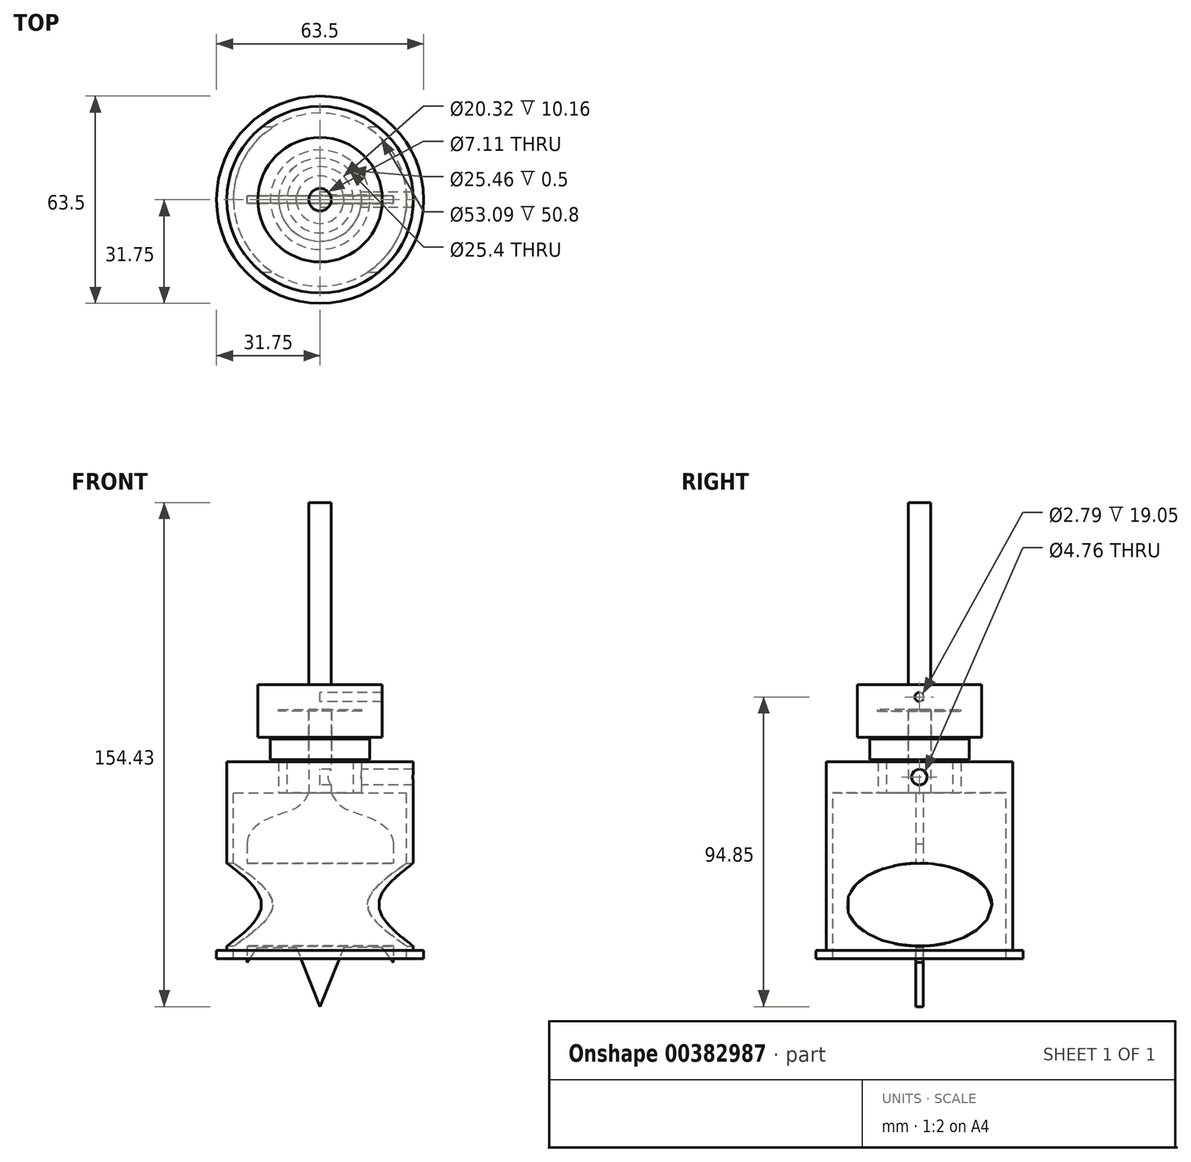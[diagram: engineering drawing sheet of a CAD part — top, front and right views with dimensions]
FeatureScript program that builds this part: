
annotation { "Feature Type Name" : "Feature", "Feature Type Description" : "" }
export const myFeature = defineFeature(function(context is Context, id is Id, definition is map)
    precondition{}
    {
        {
            var Q0;
            Q0=qCreatedBy(makeId("Top.planeOp"),FACE);
            var sketch = newSketch(context, id + "F0", { "sketchPlane" : qUnion([Q0])});
            skCircle(sketch, "E0", {"center": v(0, 0) * mm, "radius": 3.43 * mm});
            skSolve(sketch);
        }
        {
            var Q0;
            Q0 = qSketchRegion(id + "F0", true);
            extrude(context, id + "F1", {"entities" : qUnion([Q0]), "depth" : 50.8 * mm, "hasSecondDirection" : true, "secondDirectionOppositeDirection" : true, "secondDirectionDepth" : 38.1 * mm});
        }
        {
            var Q0;
            Q0=qCreatedBy(makeId("Front.planeOp"),FACE);
            var sketch = newSketch(context, id + "F2", { "sketchPlane" : qUnion([Q0])});
            skLineSegment(sketch, "E1", {"start": v(0, -33.13) * mm, "end": v(0, -75.47) * mm, "construction": true});
            skLineSegment(sketch, "E2.0", {"start": v(-3.43, -38.1) * mm, "end": v(3.43, -38.1) * mm});
            skFitSpline(sketch, "E3", {"points": [v(-3.43, -38.1) * mm, v(-12.95, -44.92) * mm, v(-22.43, -53.7) * mm], "startDerivative": vector(-13.87, -31.28) * mm, "endDerivative": vector(-0.61, -28) * mm});
            skLineSegment(sketch, "E4", {"start": v(-22.43, -53.7) * mm, "end": v(-22.43, -90.1) * mm});
            skLineSegment(sketch, "E5", {"start": v(-22.43, -90.1) * mm, "end": v(-19.06, -85.46) * mm});
            skLineSegment(sketch, "E6", {"start": v(-19.06, -85.46) * mm, "end": v(-7.28, -85.46) * mm});
            skLineSegment(sketch, "E7", {"start": v(-7.28, -85.46) * mm, "end": v(0, -103.63) * mm});
            skLineSegment(sketch, "E8.MirrorCS", {"start": v(7.28, -85.46) * mm, "end": v(0, -103.63) * mm});
            skLineSegment(sketch, "E9.MirrorCS", {"start": v(19.06, -85.46) * mm, "end": v(7.28, -85.46) * mm});
            skFitSpline(sketch, "E10.MirrorCS", {"points": [v(3.43, -38.1) * mm, v(12.95, -44.92) * mm, v(22.43, -53.7) * mm], "startDerivative": vector(13.87, -31.28) * mm, "endDerivative": vector(0.61, -28) * mm});
            skLineSegment(sketch, "E11.MirrorCS", {"start": v(22.43, -53.7) * mm, "end": v(22.43, -90.1) * mm});
            skLineSegment(sketch, "E12.MirrorCS", {"start": v(22.43, -90.1) * mm, "end": v(19.06, -85.46) * mm});
            skSolve(sketch);
        }
        {
            var Q0;
            Q0=makeQuery(id+"F2.imprint","IMPRINT",FACE,{"disambiguationData":[TD([[makeQuery(id+"F2.imprint","IMPRINT",EDGE,{"derivedFrom":sQuery(id+"F2.wireOp",EDGE,"E2.0")}),-1.0]])]});
            extrude(context, id + "F3", {"entities" : qUnion([Q0]), "operationType" : NewBodyOperationType.ADD, "depth" : 1.14 * mm, "hasSecondDirection" : true, "secondDirectionOppositeDirection" : true, "secondDirectionDepth" : 1.14 * mm});
        }
        {
            var Q0;
            Q0=qCreatedBy(makeId("Top.planeOp"),FACE);
            cPlane(context, id + "F4", {"entities" : qUnion([Q0]), "cplaneType" : CPlaneType.OFFSET, "offset" : 38.1 * mm, "oppositeDirection" : true, "width" : 152.4 * mm, "height" : 152.4 * mm});
        }
        {
            var Q0;
            Q0=qCreatedBy(id+"F4.planeOp",FACE);
            var sketch = newSketch(context, id + "F5", { "sketchPlane" : qUnion([Q0])});
            skCircle(sketch, "E13", {"center": v(0, 0) * mm, "radius": 28.58 * mm});
            skCircle(sketch, "E14", {"center": v(0, 0) * mm, "radius": 12.7 * mm});
            skSolve(sketch);
        }
        {
            var Q0;
            Q0=makeQuery(id+"F5.imprint","IMPRINT",FACE,{"disambiguationData":[TD([[makeQuery(id+"F5.imprint","IMPRINT",EDGE,{"derivedFrom":sQuery(id+"F5.wireOp",EDGE,"E13")}),1.0]])]});
            extrude(context, id + "F6", {"entities" : qUnion([Q0]), "depth" : 9.52 * mm});
        }
        {
            var Q0;
            Q0=makeQuery(id+"F6.opExtrude","CAP_FACE",FACE,{"disambiguationData":[OSD([sQuery(id+"F5.wireOp",EDGE,"E13"),sQuery(id+"F5.wireOp",EDGE,"E14")])],"isStart":true});
            var sketch = newSketch(context, id + "F7", { "sketchPlane" : qUnion([Q0])});
            skCircle(sketch, "E15.0", {"center": v(0, 0) * mm, "radius": 28.58 * mm});
            skCircle(sketch, "E16.0", {"center": v(0, 0) * mm, "radius": 26.54 * mm});
            skSolve(sketch);
        }
        {
            var Q0;
            Q0 = qSketchRegion(id + "F7", true);
            extrude(context, id + "F8", {"entities" : qUnion([Q0]), "operationType" : NewBodyOperationType.ADD, "depth" : 50.8 * mm});
        }
        {
            var Q0;
            Q0=makeQuery(id+"F8.opExtrude","CAP_FACE",FACE,{"disambiguationData":[OSD([sQuery(id+"F7.wireOp",EDGE,"E15.0"),sQuery(id+"F7.wireOp",EDGE,"E16.0")])],"isStart":false});
            var sketch = newSketch(context, id + "F9", { "sketchPlane" : qUnion([Q0])});
            skCircle(sketch, "E17.0", {"center": v(0, 0) * mm, "radius": 28.58 * mm});
            skCircle(sketch, "E18.0", {"center": v(0, 0) * mm, "radius": 31.75 * mm});
            skSolve(sketch);
        }
        {
            var Q0;
            Q0 = qSketchRegion(id + "F9", true);
            extrude(context, id + "F10", {"entities" : qUnion([Q0]), "operationType" : NewBodyOperationType.ADD, "oppositeDirection" : true, "depth" : 2.54 * mm});
        }
        {
            var Q0;
            Q0=qCreatedBy(makeId("Right.planeOp"),FACE);
            var sketch = newSketch(context, id + "F11", { "sketchPlane" : qUnion([Q0])});
            skCircle(sketch, "E19", {"center": v(0, -33.34) * mm, "radius": 2.38 * mm});
            skSolve(sketch);
        }
        {
            var Q0;
            Q0 = qSketchRegion(id + "F11", true);
            extrude(context, id + "F12", {"entities" : qUnion([Q0]), "operationType" : NewBodyOperationType.REMOVE, "endBound" : BoundingType.THROUGH_ALL, "depth" : 25.4 * mm});
        }
        {
            var Q0;
            Q0=makeQuery(id+"F6.opExtrude","CAP_FACE",FACE,{"disambiguationData":[OSD([sQuery(id+"F5.wireOp",EDGE,"E13"),sQuery(id+"F5.wireOp",EDGE,"E14")])],"isStart":true});
            var sketch = newSketch(context, id + "F13", { "sketchPlane" : qUnion([Q0])});
            skCircle(sketch, "E20.0", {"center": v(0, 0) * mm, "radius": 12.7 * mm});
            skCircle(sketch, "E21.0", {"center": v(0, 0) * mm, "radius": 10.16 * mm});
            skSolve(sketch);
        }
        {
            var Q0;
            Q0 = qSketchRegion(id + "F13", true);
            extrude(context, id + "F14", {"entities" : qUnion([Q0]), "oppositeDirection" : true, "depth" : 10.16 * mm});
        }
        {
            var Q0;
            Q0=makeQuery(id+"F14.opExtrude","CAP_FACE",FACE,{"disambiguationData":[OSD([sQuery(id+"F13.wireOp",EDGE,"E20.0"),sQuery(id+"F13.wireOp",EDGE,"E21.0")])],"isStart":false});
            var sketch = newSketch(context, id + "F15", { "sketchPlane" : qUnion([Q0])});
            skCircle(sketch, "E22.0", {"center": v(0, 0) * mm, "radius": 3.56 * mm});
            skCircle(sketch, "E23", {"center": v(0, 0) * mm, "radius": 15.24 * mm});
            skSolve(sketch);
        }
        {
            var Q0;
            Q0 = qSketchRegion(id + "F15", true);
            extrude(context, id + "F16", {"entities" : qUnion([Q0]), "operationType" : NewBodyOperationType.ADD, "depth" : 6.35 * mm});
        }
        {
            var Q0;
            Q0=makeQuery(id+"F16.opExtrude","CAP_FACE",FACE,{"disambiguationData":[OSD([sQuery(id+"F15.wireOp",EDGE,"E22.0"),sQuery(id+"F15.wireOp",EDGE,"E23")])],"isStart":false});
            var sketch = newSketch(context, id + "F17", { "sketchPlane" : qUnion([Q0])});
            skCircle(sketch, "E24", {"center": v(0, 0) * mm, "radius": 6 * mm});
            skCircle(sketch, "E25.0", {"center": v(0, 0) * mm, "radius": 3.56 * mm});
            skSolve(sketch);
        }
        {
            var Q0;
            Q0 = qSketchRegion(id + "F17", true);
            extrude(context, id + "F18", {"entities" : qUnion([Q0]), "operationType" : NewBodyOperationType.ADD, "depth" : 8.5 * mm});
        }
        {
            var Q0;
            Q0=makeQuery(id+"F18.opExtrude","CAP_FACE",FACE,{"disambiguationData":[OSD([sQuery(id+"F17.wireOp",EDGE,"E24"),sQuery(id+"F17.wireOp",EDGE,"E25.0")])],"isStart":false});
            var sketch = newSketch(context, id + "F19", { "sketchPlane" : qUnion([Q0])});
            skCircle(sketch, "E26.0", {"center": v(0, 0) * mm, "radius": 14 * mm});
            skCircle(sketch, "E27", {"center": v(0, 0) * mm, "radius": 19.05 * mm});
            skSolve(sketch);
        }
        {
            var Q0;
            Q0 = qSketchRegion(id + "F19", true);
            extrude(context, id + "F20", {"entities" : qUnion([Q0]), "oppositeDirection" : true, "depth" : 8 * mm});
        }
        {
            var Q0;
            Q0=makeQuery(id+"F18.opExtrude","CAP_FACE",FACE,{"disambiguationData":[OSD([sQuery(id+"F17.wireOp",EDGE,"E24"),sQuery(id+"F17.wireOp",EDGE,"E25.0")])],"isStart":false});
            cPlane(context, id + "F21", {"entities" : qUnion([Q0]), "cplaneType" : CPlaneType.OFFSET, "offset" : .5 * mm, "width" : 152.4 * mm, "height" : 152.4 * mm});
        }
        {
            var Q0;
            Q0=qCreatedBy(id+"F21.planeOp",FACE);
            var sketch = newSketch(context, id + "F22", { "sketchPlane" : qUnion([Q0])});
            skCircle(sketch, "E28.0", {"center": v(0, 0) * mm, "radius": 3.43 * mm});
            skCircle(sketch, "E29", {"center": v(0, 0) * mm, "radius": 19.05 * mm});
            skSolve(sketch);
        }
        {
            var Q0;
            Q0=qCreatedBy(makeId("Right.planeOp"),FACE);
            var sketch = newSketch(context, id + "F23", { "sketchPlane" : qUnion([Q0])});
            skCircle(sketch, "E30", {"center": v(0, -8.78) * mm, "radius": 1.4 * mm});
            skSolve(sketch);
        }
        {
            var Q0;
            Q0=qCreatedBy(makeId("Right.planeOp"),FACE);
            var sketch = newSketch(context, id + "F24", { "sketchPlane" : qUnion([Q0])});
            skEllipse(sketch, "E31", {"center": v(0, -72.4) * mm, "majorRadius": 22.23 * mm, "minorRadius": 12.7 * mm, "majorAxis": v(1, 0)});
            skSolve(sketch);
        }
        {
            var Q0;
            Q0 = qSketchRegion(id + "F24", true);
            extrude(context, id + "F25", {"entities" : qUnion([Q0]), "operationType" : NewBodyOperationType.REMOVE, "endBound" : BoundingType.THROUGH_ALL, "depth" : 25.4 * mm, "hasSecondDirection" : true, "secondDirectionBound" : SecondDirectionBoundingType.THROUGH_ALL, "secondDirectionOppositeDirection" : true, "secondDirectionDepth" : 25.4 * mm});
        }
        {
            var Q0;
            Q0=makeQuery(id+"F18.opExtrude","CAP_FACE",FACE,{"disambiguationData":[OSD([sQuery(id+"F17.wireOp",EDGE,"E24"),sQuery(id+"F17.wireOp",EDGE,"E25.0")])],"isStart":false});
            var sketch = newSketch(context, id + "F26", { "sketchPlane" : qUnion([Q0])});
            skCircle(sketch, "E32", {"center": v(0, 0) * mm, "radius": 14 * mm});
            skCircle(sketch, "E33", {"center": v(0, 0) * mm, "radius": 6 * mm});
            skSolve(sketch);
        }
        {
            var Q0;
            Q0 = qSketchRegion(id + "F26", true);
            extrude(context, id + "F27", {"entities" : qUnion([Q0]), "oppositeDirection" : true, "depth" : 8 * mm});
        }
        {
            var Q0;
            Q0=qCreatedBy(id+"F21.planeOp",FACE);
            var sketch = newSketch(context, id + "F28", { "sketchPlane" : qUnion([Q0])});
            skCircle(sketch, "E34.0", {"center": v(0, 0) * mm, "radius": 19.05 * mm});
            skCircle(sketch, "E35.0", {"center": v(0, 0) * mm, "radius": 14 * mm});
            skSolve(sketch);
        }
        {
            var Q0;
            Q0=makeQuery(id+"F28.imprint","IMPRINT",FACE,{"disambiguationData":[TD([[makeQuery(id+"F28.imprint","IMPRINT",EDGE,{"derivedFrom":sQuery(id+"F28.wireOp",EDGE,"E34.0")}),1.0]])]});
            extrude(context, id + "F29", {"entities" : qUnion([Q0]), "operationType" : NewBodyOperationType.ADD, "endBound" : BoundingType.UP_TO_NEXT, "oppositeDirection" : true, "depth" : 25.4 * mm});
        }
        {
            var Q0;
            Q0 = qSketchRegion(id + "F22", true);
            extrude(context, id + "F30", {"entities" : qUnion([Q0]), "operationType" : NewBodyOperationType.ADD, "depth" : 7.62 * mm});
        }
        {
            var Q0;
            Q0 = qSketchRegion(id + "F23", true);
            extrude(context, id + "F31", {"entities" : qUnion([Q0]), "operationType" : NewBodyOperationType.REMOVE, "depth" : 25.4 * mm});
        }
        {
            var Q0;
            Q0=makeQuery(id+"F30.opExtrude","CAP_FACE",FACE,{"disambiguationData":[OSD([sQuery(id+"F22.wireOp",EDGE,"E28.0"),sQuery(id+"F22.wireOp",EDGE,"E29")])],"isStart":true});
            var sketch = newSketch(context, id + "F32", { "sketchPlane" : qUnion([Q0])});
            skCircle(sketch, "E36", {"center": v(0, 0) * mm, "radius": 12.73 * mm});
            skCircle(sketch, "E37.0", {"center": v(0, 0) * mm, "radius": 14 * mm});
            skSolve(sketch);
        }
        {
            var Q0;
            Q0 = qSketchRegion(id + "F32", true);
            extrude(context, id + "F33", {"entities" : qUnion([Q0]), "operationType" : NewBodyOperationType.ADD, "depth" : .5 * mm});
        }
        {
            var Q0;
            Q0=makeQuery(id+"F16.opExtrude","CAP_FACE",FACE,{"disambiguationData":[OSD([sQuery(id+"F15.wireOp",EDGE,"E22.0"),sQuery(id+"F15.wireOp",EDGE,"E23")])],"isStart":false});
            var sketch = newSketch(context, id + "F34", { "sketchPlane" : qUnion([Q0])});
            skCircle(sketch, "E38", {"center": v(0, 0) * mm, "radius": 7.27 * mm});
            skCircle(sketch, "E39.0", {"center": v(0, 0) * mm, "radius": 6 * mm});
            skSolve(sketch);
        }
        {
            var Q0;
            Q0 = qSketchRegion(id + "F34", true);
            extrude(context, id + "F35", {"entities" : qUnion([Q0]), "operationType" : NewBodyOperationType.ADD, "depth" : .5 * mm});
        }
    });
